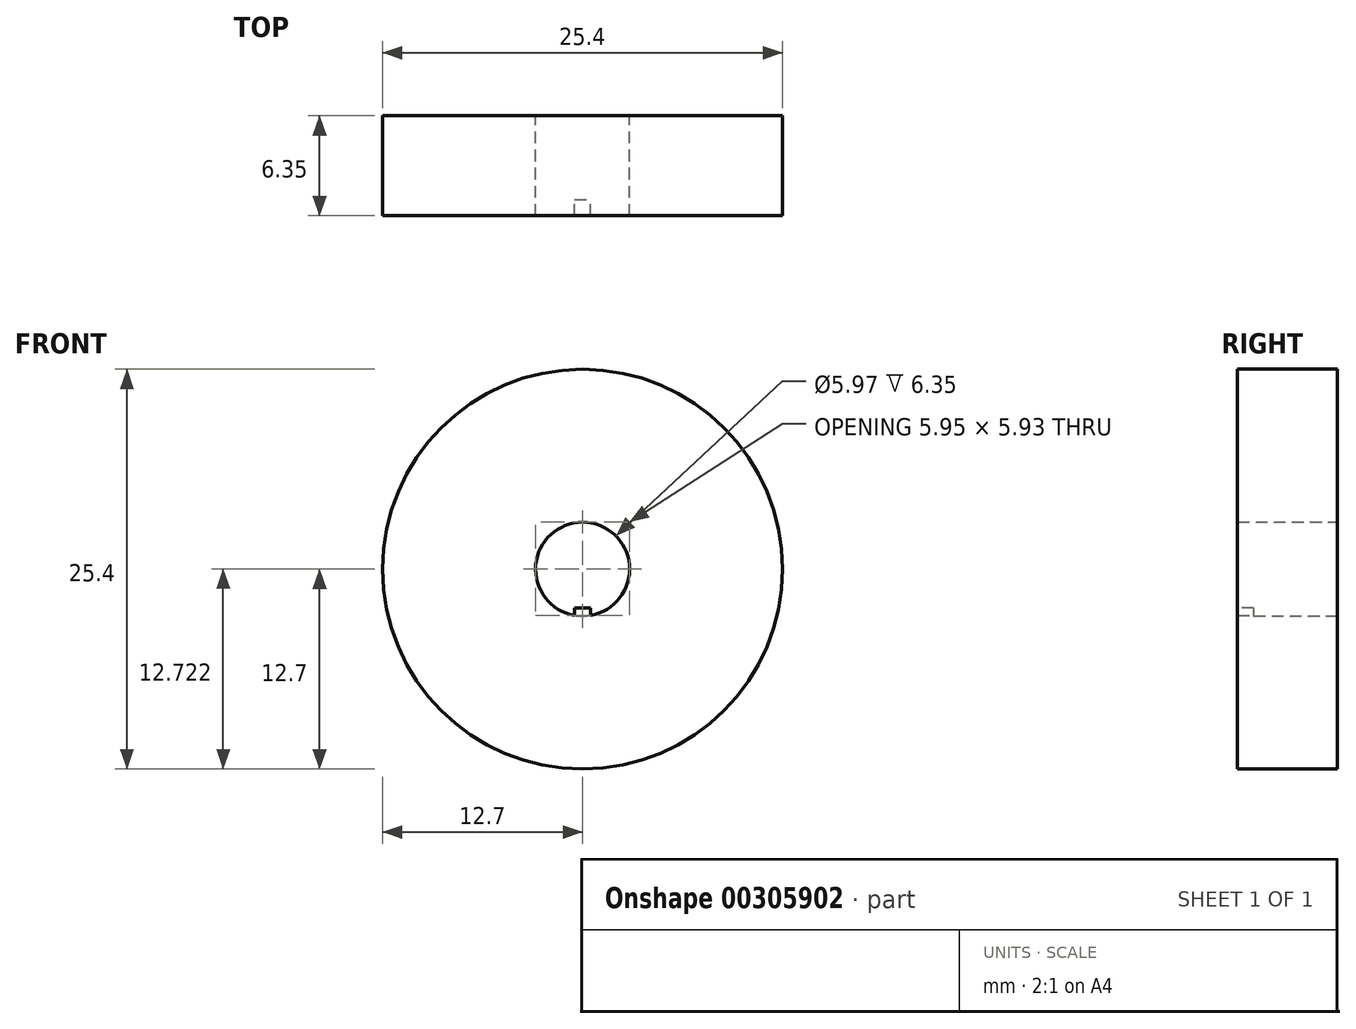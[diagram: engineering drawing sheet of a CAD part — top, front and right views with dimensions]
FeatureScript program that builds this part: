
annotation { "Feature Type Name" : "Feature", "Feature Type Description" : "" }
export const myFeature = defineFeature(function(context is Context, id is Id, definition is map)
    precondition{}
    {
        {
            var Q0;
            Q0=qCreatedBy(makeId("Front.planeOp"),FACE);
            var sketch = newSketch(context, id + "F0", { "sketchPlane" : qUnion([Q0])});
            skCircle(sketch, "E0", {"center": v(0, 0) * mm, "radius": 12.7 * mm});
            skCircle(sketch, "E1", {"center": v(0, 0) * mm, "radius": 2.98 * mm});
            skSolve(sketch);
        }
        {
            var Q0;
            Q0=makeQuery(id+"F0.imprint","IMPRINT",FACE,{"disambiguationData":[TD([[makeQuery(id+"F0.imprint","IMPRINT",EDGE,{"derivedFrom":sQuery(id+"F0.wireOp",EDGE,"E0")}),1.0]])]});
            extrude(context, id + "F1", {"entities" : qUnion([Q0]), "depth" : 6.35 * mm});
        }
        {
            var Q0;
            Q0=makeQuery(id+"F1.opExtrude","CAP_FACE",FACE,{"disambiguationData":[OSD([sQuery(id+"F0.wireOp",EDGE,"E0"),sQuery(id+"F0.wireOp",EDGE,"E1")])],"isStart":false});
            var sketch = newSketch(context, id + "F2", { "sketchPlane" : qUnion([Q0])});
            skLineSegment(sketch, "E2.bottom", {"start": v(-0.5, -2.48) * mm, "end": v(0.5, -2.48) * mm});
            skLineSegment(sketch, "E2.top", {"start": v(-0.5, -3.5) * mm, "end": v(0.5, -3.5) * mm});
            skLineSegment(sketch, "E2.left", {"start": v(-0.5, -2.48) * mm, "end": v(-0.5, -3.5) * mm});
            skLineSegment(sketch, "E2.right", {"start": v(0.5, -2.48) * mm, "end": v(0.5, -3.5) * mm});
            skPoint(sketch, "E2.middle", {"position": v(0, -2.98) * mm});
            skSolve(sketch);
        }
        {
            var Q0;
            Q0 = qSketchRegion(id + "F2", true);
            extrude(context, id + "F3", {"entities" : qUnion([Q0]), "operationType" : NewBodyOperationType.ADD, "oppositeDirection" : true, "depth" : 1.02 * mm});
        }
    });
